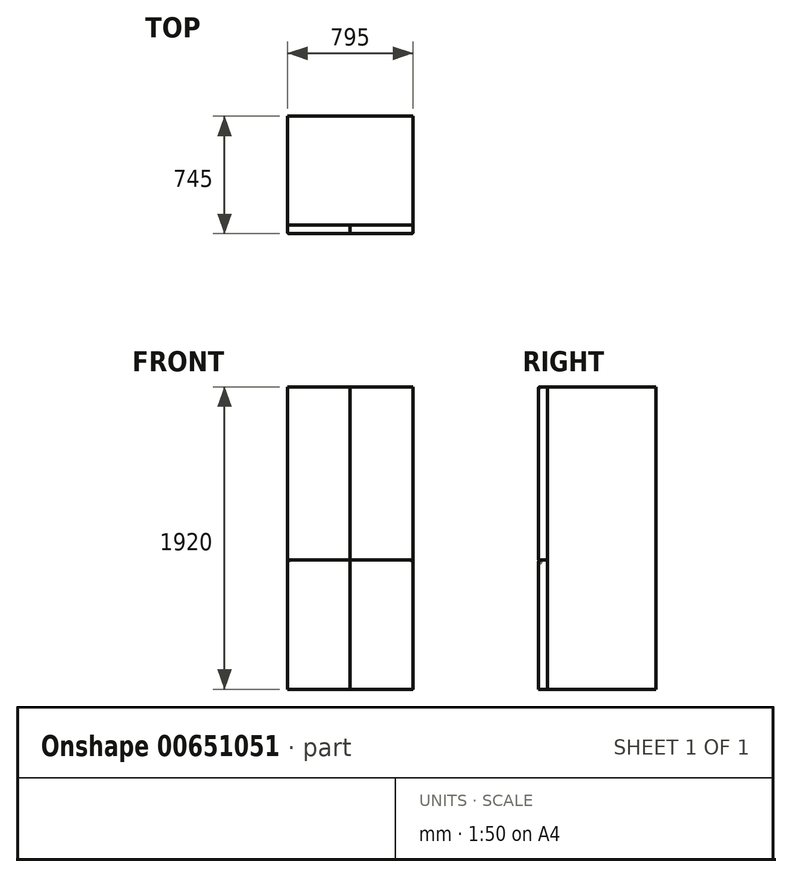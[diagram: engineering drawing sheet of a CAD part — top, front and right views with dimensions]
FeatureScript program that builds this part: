
annotation { "Feature Type Name" : "Feature", "Feature Type Description" : "" }
export const myFeature = defineFeature(function(context is Context, id is Id, definition is map)
    precondition{}
    {
        {
            var Q0;
            Q0=qCreatedBy(makeId("Top.planeOp"),FACE);
            var sketch = newSketch(context, id + "F0", { "sketchPlane" : qUnion([Q0])});
            skLineSegment(sketch, "E0.bottom", {"start": v(0, 0) * mm, "end": v(-795, 0) * mm});
            skLineSegment(sketch, "E0.top", {"start": v(0, 690) * mm, "end": v(-795, 690) * mm});
            skLineSegment(sketch, "E0.left", {"start": v(0, 0) * mm, "end": v(0, 690) * mm});
            skLineSegment(sketch, "E0.right", {"start": v(-795, 0) * mm, "end": v(-795, 690) * mm});
            skLineSegment(sketch, "E1.bottom", {"start": v(-795, 0) * mm, "end": v(-397.5, 0) * mm});
            skLineSegment(sketch, "E1.top", {"start": v(-795, -55) * mm, "end": v(-397.5, -55) * mm});
            skLineSegment(sketch, "E1.left", {"start": v(-795, 0) * mm, "end": v(-795, -55) * mm});
            skLineSegment(sketch, "E1.right", {"start": v(-397.5, 0) * mm, "end": v(-397.5, -55) * mm});
            skLineSegment(sketch, "E2.bottom", {"start": v(-397.5, 0) * mm, "end": v(0, 0) * mm});
            skLineSegment(sketch, "E2.top", {"start": v(-397.5, -55) * mm, "end": v(0, -55) * mm});
            skLineSegment(sketch, "E2.right", {"start": v(0, 0) * mm, "end": v(0, -55) * mm});
            skSolve(sketch);
        }
        {
            var Q0;
            Q0=makeQuery(id+"F0.imprint","IMPRINT",FACE,{"disambiguationData":[TD([[makeQuery(id+"F0.imprint","IMPRINT",EDGE,{"derivedFrom":sQuery(id+"F0.wireOp",EDGE,"E0.top")}),1.0]])]});
            extrude(context, id + "F1", {"entities" : qUnion([Q0]), "depth" : 1920 * mm, "offsetDistance" : 25 * mm});
        }
        {
            var Q0;
            Q0=makeQuery(id+"F0.imprint","IMPRINT",FACE,{"disambiguationData":[TD([[makeQuery(id+"F0.imprint","IMPRINT",EDGE,{"derivedFrom":sQuery(id+"F0.wireOp",EDGE,"E1.top")}),1.0]])]});
            extrude(context, id + "F2", {"entities" : qUnion([Q0]), "depth" : 820 * mm, "offsetDistance" : 25 * mm});
        }
        {
            var Q0;
            {var subQ0=sQuery(id+"F0.wireOp",EDGE,"E1.right");Q0=makeQuery(id+"F0.imprint","IMPRINT",FACE,{"disambiguationData":[TD([[makeQuery(id+"F0.imprint","IMPRINT",EDGE,{"derivedFrom":subQ0}),1.0]])]});}
            extrude(context, id + "F3", {"entities" : qUnion([Q0]), "depth" : 820 * mm, "offsetDistance" : 25 * mm});
        }
        {
            var Q0;
            Q0=makeQuery(id+"F2.opExtrude","CAP_FACE",FACE,{"disambiguationData":[OSD([sQuery(id+"F0.wireOp",EDGE,"E0.bottom"),sQuery(id+"F0.wireOp",EDGE,"E1.top"),sQuery(id+"F0.wireOp",EDGE,"E1.left"),sQuery(id+"F0.wireOp",EDGE,"E1.right")])],"isStart":false});
            var sketch = newSketch(context, id + "F4", { "sketchPlane" : qUnion([Q0])});
            skSolve(sketch);
        }
        {
            var Q0;
            Q0 = qSketchRegion(id + "F4", true);
            var Q1;
            Q1=makeQuery(id+"F4.imprint","IMPRINT",FACE,{"disambiguationData":[TD([[makeQuery(id+"F4.imprint","IMPRINT",EDGE,{"derivedFrom":makeQuery(id+"F2.opExtrude","CAP_EDGE",EDGE,{"disambiguationData":[OSD([sQuery(id+"F0.wireOp",EDGE,"E0.bottom")])],"isStart":false})}),1.0]])]});
            extrude(context, id + "F5", {"entities" : qUnion([Q0, Q1]), "depth" : 1100 * mm, "offsetDistance" : 25 * mm});
        }
        {
            var Q0;
            Q0=makeQuery(id+"F3.opExtrude","CAP_FACE",FACE,{"disambiguationData":[OSD([sQuery(id+"F0.wireOp",EDGE,"E0.bottom"),sQuery(id+"F0.wireOp",EDGE,"E1.right"),sQuery(id+"F0.wireOp",EDGE,"E2.top"),sQuery(id+"F0.wireOp",EDGE,"E2.right")])],"isStart":false});
            var sketch = newSketch(context, id + "F6", { "sketchPlane" : qUnion([Q0])});
            skSolve(sketch);
        }
        {
            var Q0;
            Q0 = qSketchRegion(id + "F6", true);
            var Q1;
            Q1=makeQuery(id+"F6.imprint","IMPRINT",FACE,{"disambiguationData":[TD([[makeQuery(id+"F6.imprint","IMPRINT",EDGE,{"derivedFrom":makeQuery(id+"F3.opExtrude","CAP_EDGE",EDGE,{"disambiguationData":[OSD([sQuery(id+"F0.wireOp",EDGE,"E0.bottom")])],"isStart":false})}),1.0]])]});
            extrude(context, id + "F7", {"entities" : qUnion([Q0, Q1]), "depth" : 1100 * mm, "offsetDistance" : 25 * mm});
        }
        {
            var Q0;
            Q0=makeQuery(id+"F5.opExtrude","CAP_EDGE",EDGE,{"disambiguationData":[OSD([sQuery(id+"F0.wireOp",EDGE,"E1.top")])],"isStart":false});
            var Q1;
            Q1=makeQuery(id+"F7.opExtrude","CAP_EDGE",EDGE,{"disambiguationData":[OSD([sQuery(id+"F0.wireOp",EDGE,"E2.top")])],"isStart":false});
            var Q2;
            Q2=makeQuery(id+"F7.opExtrude","SWEPT_EDGE",EDGE,{"disambiguationData":[OSD([sQuery(id+"F0.wireOp",EDGE,"E2.top"),sQuery(id+"F0.wireOp",EDGE,"E2.right")])]});
            var Q3;
            Q3=makeQuery(id+"F5.opExtrude","SWEPT_EDGE",EDGE,{"disambiguationData":[OSD([sQuery(id+"F0.wireOp",EDGE,"E1.top"),sQuery(id+"F0.wireOp",EDGE,"E1.left")])]});
            var Q4;
            Q4=makeQuery(id+"F2.opExtrude","SWEPT_EDGE",EDGE,{"disambiguationData":[OSD([sQuery(id+"F0.wireOp",EDGE,"E1.top"),sQuery(id+"F0.wireOp",EDGE,"E1.left")])]});
            var Q5;
            Q5=makeQuery(id+"F3.opExtrude","SWEPT_EDGE",EDGE,{"disambiguationData":[OSD([sQuery(id+"F0.wireOp",EDGE,"E2.top"),sQuery(id+"F0.wireOp",EDGE,"E2.right")])]});
            fillet(context, id + "F8", {"entities" : qUnion([Q0, Q1, Q2, Q3, Q4, Q5]), "radius" : 5 * mm, "tangentPropagation" : true, "allowEdgeOverflow" : false});
        }
        {
            var Q0;
            Q0=makeQuery(id+"F2.opExtrude","CAP_EDGE",EDGE,{"disambiguationData":[OSD([sQuery(id+"F0.wireOp",EDGE,"E1.top")])],"isStart":false});
            var Q1;
            Q1=makeQuery(id+"F3.opExtrude","CAP_EDGE",EDGE,{"disambiguationData":[OSD([sQuery(id+"F0.wireOp",EDGE,"E2.top")])],"isStart":false});
            var Q2;
            Q2=makeQuery(id+"F7.opExtrude","SWEPT_EDGE",EDGE,{"disambiguationData":[OSD([sQuery(id+"F0.wireOp",EDGE,"E1.right"),sQuery(id+"F0.wireOp",EDGE,"E2.top")])]});
            fillet(context, id + "F9", {"entities" : qUnion([Q0, Q1, Q2]), "radius" : 10 * mm, "tangentPropagation" : true, "allowEdgeOverflow" : false});
        }
    });
